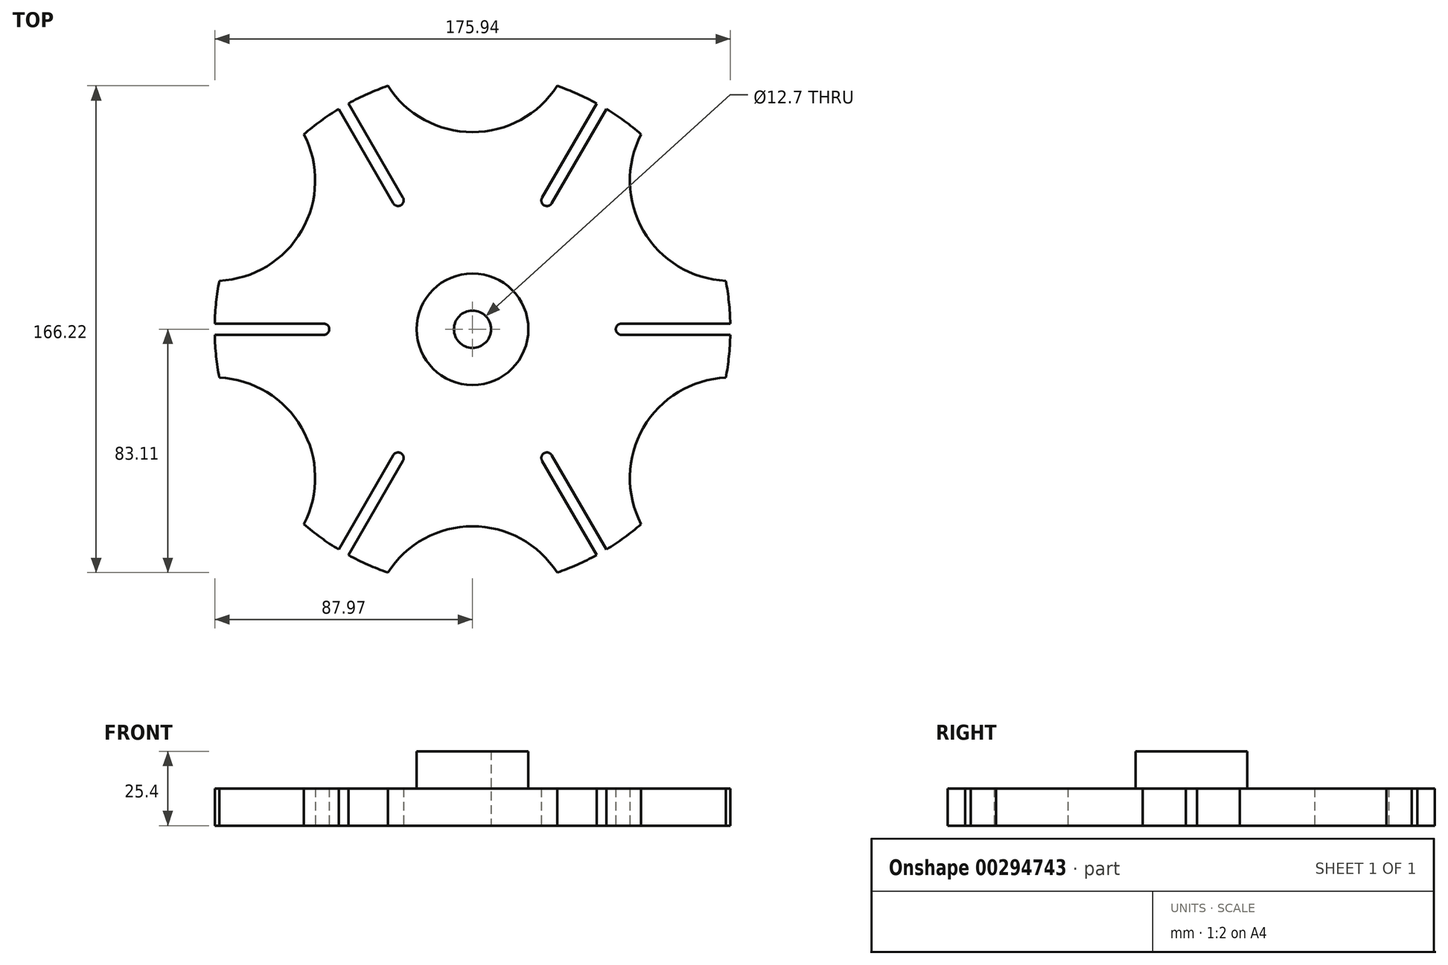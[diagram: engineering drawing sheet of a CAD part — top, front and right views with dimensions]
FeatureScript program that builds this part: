
annotation { "Feature Type Name" : "Feature", "Feature Type Description" : "" }
export const myFeature = defineFeature(function(context is Context, id is Id, definition is map)
    precondition{}
    {
        {
            var Q0;
            Q0=qCreatedBy(makeId("Top.planeOp"),FACE);
            var sketch = newSketch(context, id + "F0", { "sketchPlane" : qUnion([Q0])});
            skLineSegment(sketch, "E0", {"start": v(0, 50.8) * mm, "end": v(0, 0) * mm});
            skLineSegment(sketch, "E1", {"start": v(0, 0) * mm, "end": v(50.8, 0) * mm});
            skLineSegment(sketch, "E2", {"start": v(87.99, 0) * mm, "end": v(0, 50.8) * mm});
            skArc(sketch, "E3", {"start": v(87.97, 1.9) * mm, "mid": v(76.2, 44) * mm, "end": v(45.63, 75.23) * mm});
            skPoint(sketch, "E4", {"position": v(50.8, 0) * mm});
            skLineSegment(sketch, "E5.bottom", {"start": v(50.8, 1.9) * mm, "end": v(87.97, 1.9) * mm});
            skLineSegment(sketch, "E5.top", {"start": v(50.8, -1.9) * mm, "end": v(87.97, -1.9) * mm});
            skArc(sketch, "E6", {"start": v(50.8, 1.9) * mm, "mid": v(48.9, 0) * mm, "end": v(50.8, -1.9) * mm});
            skCircle(sketch, "E7", {"center": v(87.99, -50.8) * mm, "radius": 34.3 * mm});
            skLineSegment(sketch, "E8.bottom", {"start": v(-50.78, 1.9) * mm, "end": v(-87.97, 1.9) * mm});
            skLineSegment(sketch, "E8.top", {"start": v(-50.78, -1.9) * mm, "end": v(-87.97, -1.9) * mm});
            skArc(sketch, "E9", {"start": v(-50.78, -1.9) * mm, "mid": v(-48.87, 0) * mm, "end": v(-50.78, 1.9) * mm});
            skArc(sketch, "E10.trimOffspring", {"start": v(-87.97, -1.9) * mm, "mid": v(-84.74, -23.7) * mm, "end": v(-76.2, -44) * mm});
            skLineSegment(sketch, "E11", {"start": v(-45.63, 75.23) * mm, "end": v(-27.04, 43.02) * mm});
            skLineSegment(sketch, "E12", {"start": v(-23.74, 44.93) * mm, "end": v(-42.33, 77.13) * mm});
            skArc(sketch, "E13", {"start": v(-27.04, 43.02) * mm, "mid": v(-24.44, 42.33) * mm, "end": v(-23.74, 44.93) * mm});
            skArc(sketch, "E14.trimOffspring", {"start": v(-45.63, 75.23) * mm, "mid": v(-76.2, 44) * mm, "end": v(-87.97, 1.9) * mm});
            skArc(sketch, "E15.cCircle", {"start": v(-45.63, 75.23) * mm, "mid": v(-85.23, 21.85) * mm, "end": v(-76.2, -44) * mm, "construction": true});
            skLineSegment(sketch, "E15.0", {"start": v(-50.8, 87.99) * mm, "end": v(50.8, 87.99) * mm});
            skLineSegment(sketch, "E15.1", {"start": v(50.8, 87.99) * mm, "end": v(101.6, 0) * mm});
            skLineSegment(sketch, "E15.2", {"start": v(101.6, 0) * mm, "end": v(50.8, -87.99) * mm});
            skLineSegment(sketch, "E15.3", {"start": v(50.8, -87.99) * mm, "end": v(-50.8, -87.99) * mm});
            skLineSegment(sketch, "E15.4", {"start": v(-50.8, -87.99) * mm, "end": v(-101.6, 0) * mm});
            skLineSegment(sketch, "E15.5", {"start": v(-101.6, 0) * mm, "end": v(-50.8, 87.99) * mm});
            skPoint(sketch, "E15.0.midPoint", {"position": v(0, 87.99) * mm});
            skLineSegment(sketch, "E16", {"start": v(50.8, -87.99) * mm, "end": v(-25.39, 43.98) * mm, "construction": true});
            skLineSegment(sketch, "E17", {"start": v(-50.8, -87.99) * mm, "end": v(25.39, 43.98) * mm, "construction": true});
            skLineSegment(sketch, "E18.trimOffspring", {"start": v(-43.98, 76.18) * mm, "end": v(-50.8, 87.99) * mm, "construction": true});
            skLineSegment(sketch, "E19", {"start": v(42.33, 77.13) * mm, "end": v(23.74, 44.93) * mm});
            skLineSegment(sketch, "E20", {"start": v(27.04, 43.02) * mm, "end": v(45.63, 75.23) * mm});
            skArc(sketch, "E21", {"start": v(23.74, 44.93) * mm, "mid": v(24.44, 42.33) * mm, "end": v(27.04, 43.02) * mm});
            skLineSegment(sketch, "E22", {"start": v(43.98, 76.18) * mm, "end": v(44, 76.2) * mm});
            skLineSegment(sketch, "E23.trimOffspring", {"start": v(43.98, 76.18) * mm, "end": v(50.8, 87.99) * mm, "construction": true});
            skArc(sketch, "E24.trimOffspring", {"start": v(42.33, 77.13) * mm, "mid": v(0, 87.99) * mm, "end": v(-42.33, 77.13) * mm, "construction": true});
            skArc(sketch, "E25.trimOffspring", {"start": v(42.33, 77.13) * mm, "mid": v(0, 87.99) * mm, "end": v(-42.33, 77.13) * mm});
            skLineSegment(sketch, "E26.MirrorCS", {"start": v(-45.63, -75.23) * mm, "end": v(-27.04, -43.02) * mm});
            skLineSegment(sketch, "E27.MirrorCS", {"start": v(-23.74, -44.93) * mm, "end": v(-42.33, -77.13) * mm});
            skArc(sketch, "E28.MirrorCS", {"start": v(-27.04, -43.02) * mm, "mid": v(-24.44, -42.33) * mm, "end": v(-23.74, -44.93) * mm});
            skArc(sketch, "E29.MirrorCS", {"start": v(23.74, -44.93) * mm, "mid": v(24.44, -42.33) * mm, "end": v(27.04, -43.02) * mm});
            skLineSegment(sketch, "E30.MirrorCS", {"start": v(27.04, -43.02) * mm, "end": v(45.63, -75.23) * mm});
            skLineSegment(sketch, "E31.MirrorCS", {"start": v(42.33, -77.13) * mm, "end": v(23.74, -44.93) * mm});
            skArc(sketch, "E32.trimOffspring", {"start": v(45.63, -75.23) * mm, "mid": v(87.99, 0) * mm, "end": v(45.63, 75.23) * mm, "construction": true});
            skArc(sketch, "E33.trimOffspring", {"start": v(45.63, -75.23) * mm, "mid": v(76.2, -44) * mm, "end": v(87.97, -1.9) * mm});
            skArc(sketch, "E34.trimOffspring", {"start": v(-76.2, -44) * mm, "mid": v(-62.89, -61.54) * mm, "end": v(-45.63, -75.23) * mm});
            skArc(sketch, "E35.trimOffspring", {"start": v(-42.33, -77.13) * mm, "mid": v(0, -87.99) * mm, "end": v(42.33, -77.13) * mm});
            skArc(sketch, "E36.trimOffspring", {"start": v(-42.33, -77.13) * mm, "mid": v(0, -87.99) * mm, "end": v(42.33, -77.13) * mm, "construction": true});
            skLineSegment(sketch, "E37", {"start": v(45.63, -75.23) * mm, "end": v(87.99, -50.8) * mm});
            skLineSegment(sketch, "E38", {"start": v(87.99, -50.8) * mm, "end": v(87.97, -1.9) * mm});
            skCircle(sketch, "E39.MirrorC", {"center": v(-87.99, 50.8) * mm, "radius": 34.3 * mm});
            skCircle(sketch, "E40.MirrorC", {"center": v(0, 101.6) * mm, "radius": 34.3 * mm});
            skCircle(sketch, "E41.MirrorC", {"center": v(87.99, 50.8) * mm, "radius": 34.3 * mm});
            skCircle(sketch, "E42.MirrorC", {"center": v(-87.99, -50.8) * mm, "radius": 34.3 * mm});
            skCircle(sketch, "E43.MirrorC", {"center": v(0, -101.6) * mm, "radius": 34.3 * mm});
            skCircle(sketch, "E44", {"center": v(0, 0) * mm, "radius": 6.35 * mm});
            skSolve(sketch);
        }
        {
            var Q0;
            {var subQ3=sQuery(id+"F0.wireOp",EDGE,"E2");var subQ5=sQuery(id+"F0.wireOp",EDGE,"E0");var subQ6=makeQuery(id+"F0.imprint","INTERSECT",VERTEX,{"derivedFrom":[subQ5,subQ3]});Q0=makeQuery(id+"F0.imprint","IMPRINT",FACE,{"disambiguationData":[TD([[makeQuery(id+"F0.imprint","IMPRINT",EDGE,{"disambiguationData":[TD([[subQ6,-1.0]])],"derivedFrom":subQ5}),1.0]])]});}
            var Q1;
            {var subQ10=sQuery(id+"F0.wireOp",EDGE,"E5.top");Q1=makeQuery(id+"F0.imprint","IMPRINT",FACE,{"disambiguationData":[TD([[makeQuery(id+"F0.imprint","IMPRINT",EDGE,{"derivedFrom":subQ10}),-1.0]])]});}
            extrude(context, id + "F1", {"entities" : qUnion([Q0, Q1]), "depth" : 12.7 * mm});
        }
        {
            var Q0;
            Q0=makeQuery(id+"F1.opExtrude","CAP_FACE",FACE,{"disambiguationData":[OSD([sQuery(id+"F0.wireOp",EDGE,"E3"),sQuery(id+"F0.wireOp",EDGE,"E5.bottom"),sQuery(id+"F0.wireOp",EDGE,"E5.top"),sQuery(id+"F0.wireOp",EDGE,"E6"),sQuery(id+"F0.wireOp",EDGE,"E7"),sQuery(id+"F0.wireOp",EDGE,"E8.bottom"),sQuery(id+"F0.wireOp",EDGE,"E8.top"),sQuery(id+"F0.wireOp",EDGE,"E9"),sQuery(id+"F0.wireOp",EDGE,"E10.trimOffspring"),sQuery(id+"F0.wireOp",EDGE,"E11"),sQuery(id+"F0.wireOp",EDGE,"E12"),sQuery(id+"F0.wireOp",EDGE,"E13"),sQuery(id+"F0.wireOp",EDGE,"E14.trimOffspring"),sQuery(id+"F0.wireOp",EDGE,"E19"),sQuery(id+"F0.wireOp",EDGE,"E20"),sQuery(id+"F0.wireOp",EDGE,"E21"),sQuery(id+"F0.wireOp",EDGE,"E25.trimOffspring"),sQuery(id+"F0.wireOp",EDGE,"E26.MirrorCS"),sQuery(id+"F0.wireOp",EDGE,"E27.MirrorCS"),sQuery(id+"F0.wireOp",EDGE,"E28.MirrorCS"),sQuery(id+"F0.wireOp",EDGE,"E29.MirrorCS"),sQuery(id+"F0.wireOp",EDGE,"E30.MirrorCS"),sQuery(id+"F0.wireOp",EDGE,"E31.MirrorCS"),sQuery(id+"F0.wireOp",EDGE,"E33.trimOffspring"),sQuery(id+"F0.wireOp",EDGE,"E34.trimOffspring"),sQuery(id+"F0.wireOp",EDGE,"E35.trimOffspring"),sQuery(id+"F0.wireOp",EDGE,"E39.MirrorC"),sQuery(id+"F0.wireOp",EDGE,"E40.MirrorC"),sQuery(id+"F0.wireOp",EDGE,"E41.MirrorC"),sQuery(id+"F0.wireOp",EDGE,"E42.MirrorC"),sQuery(id+"F0.wireOp",EDGE,"E43.MirrorC"),sQuery(id+"F0.wireOp",EDGE,"E44")])],"isStart":false});
            var sketch = newSketch(context, id + "F2", { "sketchPlane" : qUnion([Q0])});
            skCircle(sketch, "E45", {"center": v(0, 0) * mm, "radius": 6.35 * mm});
            skCircle(sketch, "E46", {"center": v(0, 0) * mm, "radius": 19.05 * mm});
            skSolve(sketch);
        }
        {
            var Q0;
            Q0=makeQuery(id+"F2.imprint","IMPRINT",FACE,{"disambiguationData":[TD([[makeQuery(id+"F2.imprint","IMPRINT",EDGE,{"derivedFrom":sQuery(id+"F2.wireOp",EDGE,"E45")}),-1.0]])]});
            extrude(context, id + "F3", {"entities" : qUnion([Q0]), "operationType" : NewBodyOperationType.ADD, "depth" : 12.7 * mm});
        }
    });
